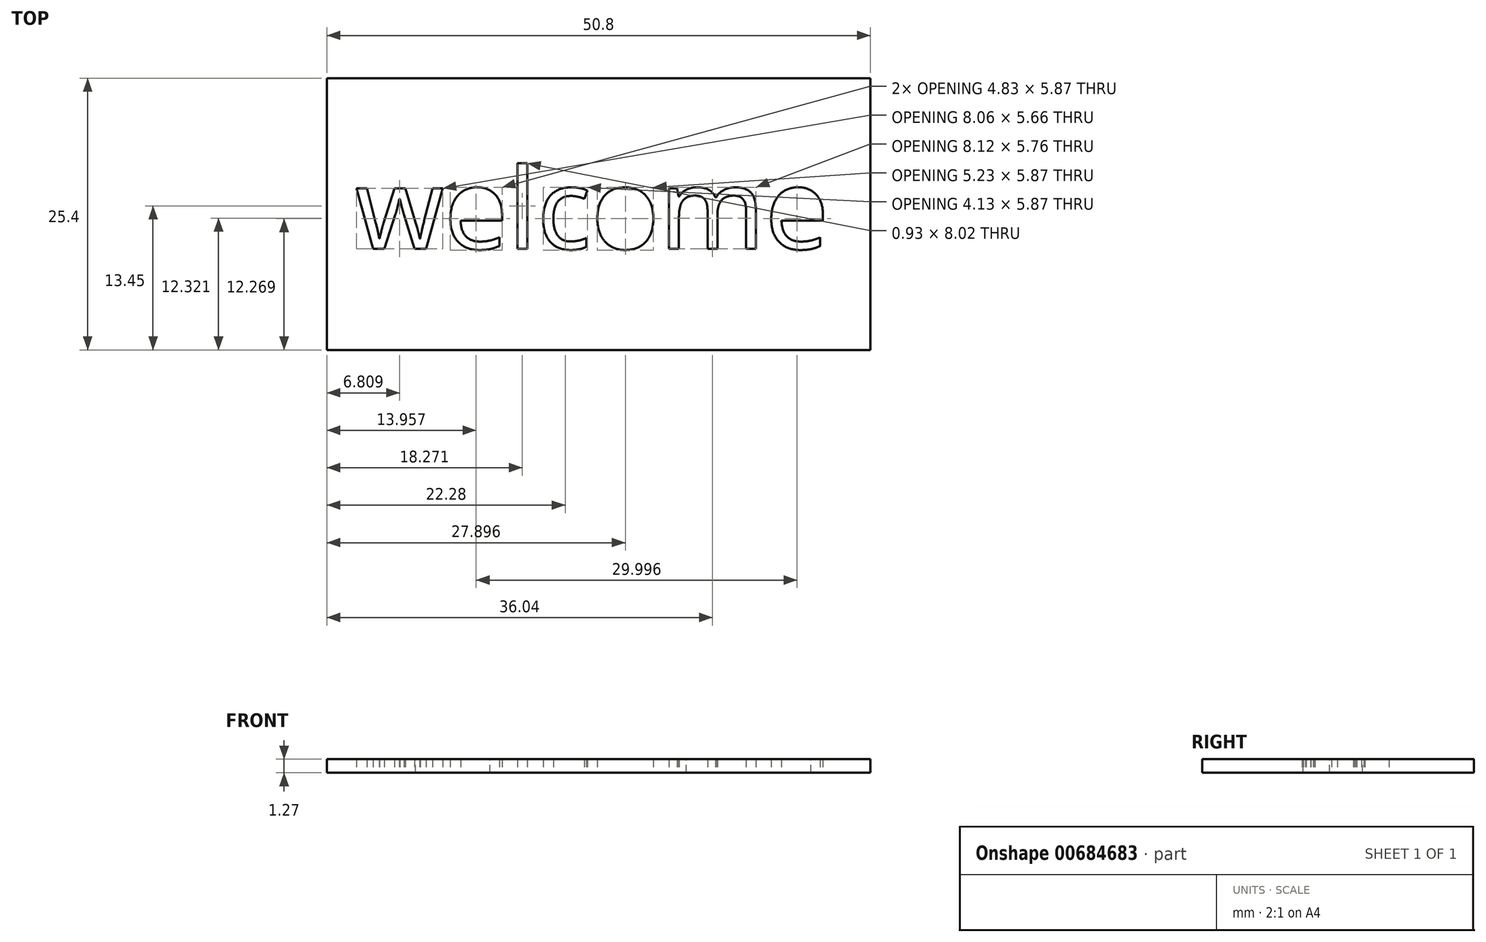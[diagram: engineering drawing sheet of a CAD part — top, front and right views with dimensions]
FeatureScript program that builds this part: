
annotation { "Feature Type Name" : "Feature", "Feature Type Description" : "" }
export const myFeature = defineFeature(function(context is Context, id is Id, definition is map)
    precondition{}
    {
        {
            var Q0;
            Q0=qCreatedBy(makeId("Top.planeOp"),FACE);
            var sketch = newSketch(context, id + "F0", { "sketchPlane" : qUnion([Q0])});
            skLineSegment(sketch, "E0.bottom", {"start": v(-23.82, 13.44) * mm, "end": v(26.98, 13.44) * mm});
            skLineSegment(sketch, "E0.top", {"start": v(-23.82, -11.96) * mm, "end": v(26.98, -11.96) * mm});
            skLineSegment(sketch, "E0.left", {"start": v(-23.82, 13.44) * mm, "end": v(-23.82, -11.96) * mm});
            skLineSegment(sketch, "E0.right", {"start": v(26.98, 13.44) * mm, "end": v(26.98, -11.96) * mm});
            skText(sketch, "E1", { "text": "welcome", "fontName": "NotoSans-Regular.ttf"});
            const initialGuessF0  = {"E1": [-0.02116, -0.00252, 1, 0, 0.0076]};
            skSetInitialGuess(sketch, initialGuessF0);
            skSolve(sketch);
        }
        {
            var Q0;
            Q0=qSketchRegion(id+"F0",true);
            extrude(context, id + "F1", {"entities" : qUnion([Q0]), "depth" : 1.27 * mm, "offsetDistance" : 25.4 * mm});
        }
    });
